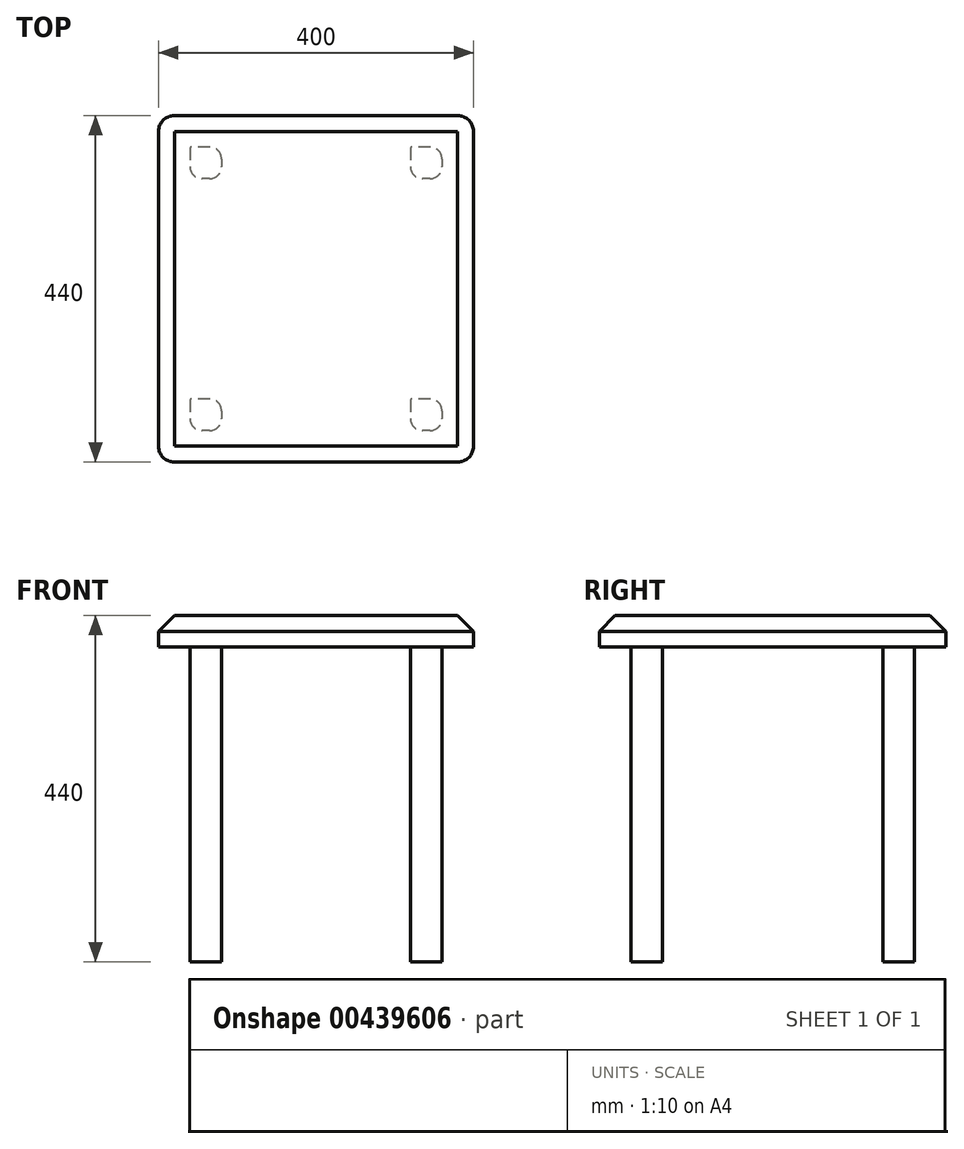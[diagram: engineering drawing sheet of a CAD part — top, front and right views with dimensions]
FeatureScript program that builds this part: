
annotation { "Feature Type Name" : "Feature", "Feature Type Description" : "" }
export const myFeature = defineFeature(function(context is Context, id is Id, definition is map)
    precondition{}
    {
        {
            var Q0;
            Q0=qCreatedBy(makeId("Top.planeOp"),FACE);
            var sketch = newSketch(context, id + "F0", { "sketchPlane" : qUnion([Q0])});
            skLineSegment(sketch, "E0.bottom", {"start": v(-177.18, 235.75) * mm, "end": v(182.82, 235.75) * mm});
            skLineSegment(sketch, "E0.top", {"start": v(-177.18, -204.25) * mm, "end": v(182.82, -204.25) * mm});
            skLineSegment(sketch, "E0.left", {"start": v(-197.18, 215.75) * mm, "end": v(-197.18, -184.25) * mm});
            skLineSegment(sketch, "E0.right", {"start": v(202.82, 215.75) * mm, "end": v(202.82, -184.25) * mm});
            skPoint(sketch, "E1.visualSharp", {"position": v(-197.18, 235.75) * mm});
            skArc(sketch, "E1.filletArc", {"start": v(-177.18, 235.75) * mm, "mid": v(-191.32, 229.9) * mm, "end": v(-197.18, 215.75) * mm});
            skPoint(sketch, "E2.visualSharp", {"position": v(202.82, 235.75) * mm});
            skArc(sketch, "E2.filletArc", {"start": v(202.82, 215.75) * mm, "mid": v(196.96, 229.9) * mm, "end": v(182.82, 235.75) * mm});
            skPoint(sketch, "E3.visualSharp", {"position": v(202.82, -204.25) * mm});
            skArc(sketch, "E3.filletArc", {"start": v(182.82, -204.25) * mm, "mid": v(196.96, -198.4) * mm, "end": v(202.82, -184.25) * mm});
            skPoint(sketch, "E4.visualSharp", {"position": v(-197.18, -204.25) * mm});
            skArc(sketch, "E4.filletArc", {"start": v(-197.18, -184.25) * mm, "mid": v(-191.32, -198.4) * mm, "end": v(-177.18, -204.25) * mm});
            skSolve(sketch);
        }
        {
            var Q0;
            Q0 = qSketchRegion(id + "F0", true);
            extrude(context, id + "F1", {"entities" : qUnion([Q0]), "depth" : 40 * mm});
        }
        {
            var Q0;
            Q0=makeQuery(id+"F1.opExtrude","CAP_FACE",FACE,{"disambiguationData":[OSD([sQuery(id+"F0.wireOp",EDGE,"E0.bottom"),sQuery(id+"F0.wireOp",EDGE,"E0.top"),sQuery(id+"F0.wireOp",EDGE,"E0.left"),sQuery(id+"F0.wireOp",EDGE,"E0.right"),sQuery(id+"F0.wireOp",EDGE,"E1.filletArc"),sQuery(id+"F0.wireOp",EDGE,"E2.filletArc"),sQuery(id+"F0.wireOp",EDGE,"E3.filletArc"),sQuery(id+"F0.wireOp",EDGE,"E4.filletArc")])],"isStart":true});
            var sketch = newSketch(context, id + "F2", { "sketchPlane" : qUnion([Q0])});
            skLineSegment(sketch, "E5.bottom", {"start": v(147.82, -195.75) * mm, "end": v(124.33, -195.75) * mm});
            skLineSegment(sketch, "E5.top", {"start": v(147.82, -155.75) * mm, "end": v(137.82, -155.75) * mm});
            skLineSegment(sketch, "E5.left", {"start": v(162.82, -180.75) * mm, "end": v(162.82, -170.75) * mm});
            skLineSegment(sketch, "E5.right", {"start": v(122.82, -194.24) * mm, "end": v(122.82, -170.75) * mm});
            skPoint(sketch, "E6.visualSharp", {"position": v(122.82, -195.75) * mm});
            skArc(sketch, "E6.filletArc", {"start": v(122.82, -194.24) * mm, "mid": v(123.26, -195.3) * mm, "end": v(124.33, -195.75) * mm});
            skPoint(sketch, "E7.visualSharp", {"position": v(162.82, -195.75) * mm});
            skArc(sketch, "E7.filletArc", {"start": v(147.82, -195.75) * mm, "mid": v(158.42, -191.36) * mm, "end": v(162.82, -180.75) * mm});
            skPoint(sketch, "E8.visualSharp", {"position": v(162.82, -155.75) * mm});
            skArc(sketch, "E8.filletArc", {"start": v(162.82, -170.75) * mm, "mid": v(158.42, -160.14) * mm, "end": v(147.82, -155.75) * mm});
            skPoint(sketch, "E9.visualSharp", {"position": v(122.82, -155.75) * mm});
            skArc(sketch, "E9.filletArc", {"start": v(137.82, -155.75) * mm, "mid": v(127.21, -160.14) * mm, "end": v(122.82, -170.75) * mm});
            skArc(sketch, "E10.0.1.0", {"start": v(147.82, 124.25) * mm, "mid": v(158.42, 128.64) * mm, "end": v(162.82, 139.25) * mm});
            skPoint(sketch, "E10.0.1.1", {"position": v(122.82, 124.25) * mm});
            skPoint(sketch, "E10.0.1.2", {"position": v(162.82, 124.25) * mm});
            skLineSegment(sketch, "E10.0.1.3", {"start": v(122.82, 125.76) * mm, "end": v(122.82, 149.25) * mm});
            skPoint(sketch, "E10.0.1.4", {"position": v(162.82, 164.25) * mm});
            skPoint(sketch, "E10.0.1.5", {"position": v(122.82, 164.25) * mm});
            skLineSegment(sketch, "E10.0.1.6", {"start": v(147.82, 124.25) * mm, "end": v(124.33, 124.25) * mm});
            skLineSegment(sketch, "E10.0.1.7", {"start": v(147.82, 164.25) * mm, "end": v(137.82, 164.25) * mm});
            skArc(sketch, "E10.0.1.8", {"start": v(162.82, 149.25) * mm, "mid": v(158.42, 159.86) * mm, "end": v(147.82, 164.25) * mm});
            skArc(sketch, "E10.0.1.9", {"start": v(137.82, 164.25) * mm, "mid": v(127.21, 159.86) * mm, "end": v(122.82, 149.25) * mm});
            skLineSegment(sketch, "E10.0.1.10", {"start": v(162.82, 139.25) * mm, "end": v(162.82, 149.25) * mm});
            skArc(sketch, "E10.0.1.11", {"start": v(122.82, 125.76) * mm, "mid": v(123.26, 124.7) * mm, "end": v(124.33, 124.25) * mm});
            skArc(sketch, "E10.1.0.0", {"start": v(-132.18, -195.75) * mm, "mid": v(-121.58, -191.36) * mm, "end": v(-117.18, -180.75) * mm});
            skPoint(sketch, "E10.1.0.1", {"position": v(-157.18, -195.75) * mm});
            skPoint(sketch, "E10.1.0.2", {"position": v(-117.18, -195.75) * mm});
            skLineSegment(sketch, "E10.1.0.3", {"start": v(-157.18, -194.24) * mm, "end": v(-157.18, -170.75) * mm});
            skPoint(sketch, "E10.1.0.4", {"position": v(-117.18, -155.75) * mm});
            skPoint(sketch, "E10.1.0.5", {"position": v(-157.18, -155.75) * mm});
            skLineSegment(sketch, "E10.1.0.6", {"start": v(-132.18, -195.75) * mm, "end": v(-155.67, -195.75) * mm});
            skLineSegment(sketch, "E10.1.0.7", {"start": v(-132.18, -155.75) * mm, "end": v(-142.18, -155.75) * mm});
            skArc(sketch, "E10.1.0.8", {"start": v(-117.18, -170.75) * mm, "mid": v(-121.58, -160.14) * mm, "end": v(-132.18, -155.75) * mm});
            skArc(sketch, "E10.1.0.9", {"start": v(-142.18, -155.75) * mm, "mid": v(-152.79, -160.14) * mm, "end": v(-157.18, -170.75) * mm});
            skLineSegment(sketch, "E10.1.0.10", {"start": v(-117.18, -180.75) * mm, "end": v(-117.18, -170.75) * mm});
            skArc(sketch, "E10.1.0.11", {"start": v(-157.18, -194.24) * mm, "mid": v(-156.74, -195.3) * mm, "end": v(-155.67, -195.75) * mm});
            skArc(sketch, "E10.1.1.0", {"start": v(-132.18, 124.25) * mm, "mid": v(-121.58, 128.64) * mm, "end": v(-117.18, 139.25) * mm});
            skPoint(sketch, "E10.1.1.1", {"position": v(-157.18, 124.25) * mm});
            skPoint(sketch, "E10.1.1.2", {"position": v(-117.18, 124.25) * mm});
            skLineSegment(sketch, "E10.1.1.3", {"start": v(-157.18, 125.76) * mm, "end": v(-157.18, 149.25) * mm});
            skPoint(sketch, "E10.1.1.4", {"position": v(-117.18, 164.25) * mm});
            skPoint(sketch, "E10.1.1.5", {"position": v(-157.18, 164.25) * mm});
            skLineSegment(sketch, "E10.1.1.6", {"start": v(-132.18, 124.25) * mm, "end": v(-155.67, 124.25) * mm});
            skLineSegment(sketch, "E10.1.1.7", {"start": v(-132.18, 164.25) * mm, "end": v(-142.18, 164.25) * mm});
            skArc(sketch, "E10.1.1.8", {"start": v(-117.18, 149.25) * mm, "mid": v(-121.58, 159.86) * mm, "end": v(-132.18, 164.25) * mm});
            skArc(sketch, "E10.1.1.9", {"start": v(-142.18, 164.25) * mm, "mid": v(-152.79, 159.86) * mm, "end": v(-157.18, 149.25) * mm});
            skLineSegment(sketch, "E10.1.1.10", {"start": v(-117.18, 139.25) * mm, "end": v(-117.18, 149.25) * mm});
            skArc(sketch, "E10.1.1.11", {"start": v(-157.18, 125.76) * mm, "mid": v(-156.74, 124.7) * mm, "end": v(-155.67, 124.25) * mm});
            skLineSegment(sketch, "E10.direction1", {"start": v(122.82, -195.75) * mm, "end": v(-157.18, -195.75) * mm, "construction": true});
            skLineSegment(sketch, "E10.direction2", {"start": v(122.82, -195.75) * mm, "end": v(122.82, 124.25) * mm, "construction": true});
            skSolve(sketch);
        }
        {
            var Q0;
            Q0=makeQuery(id+"F2.imprint","IMPRINT",FACE,{"disambiguationData":[TD([[makeQuery(id+"F2.imprint","IMPRINT",EDGE,{"derivedFrom":sQuery(id+"F2.wireOp",EDGE,"E10.1.0.0")}),1.0]])]});
            var Q1;
            Q1=makeQuery(id+"F2.imprint","IMPRINT",FACE,{"disambiguationData":[TD([[makeQuery(id+"F2.imprint","IMPRINT",EDGE,{"derivedFrom":sQuery(id+"F2.wireOp",EDGE,"E5.bottom")}),-1.0]])]});
            var Q2;
            Q2=makeQuery(id+"F2.imprint","IMPRINT",FACE,{"disambiguationData":[TD([[makeQuery(id+"F2.imprint","IMPRINT",EDGE,{"derivedFrom":sQuery(id+"F2.wireOp",EDGE,"E10.0.1.0")}),1.0]])]});
            var Q3;
            Q3=makeQuery(id+"F2.imprint","IMPRINT",FACE,{"disambiguationData":[TD([[makeQuery(id+"F2.imprint","IMPRINT",EDGE,{"derivedFrom":sQuery(id+"F2.wireOp",EDGE,"E10.1.1.0")}),1.0]])]});
            extrude(context, id + "F3", {"entities" : qUnion([Q0, Q1, Q2, Q3]), "operationType" : NewBodyOperationType.ADD, "depth" : 400 * mm});
        }
        {
            var Q0;
            Q0=makeQuery(id+"F1.opExtrude","CAP_FACE",FACE,{"disambiguationData":[OSD([sQuery(id+"F0.wireOp",EDGE,"E0.bottom"),sQuery(id+"F0.wireOp",EDGE,"E0.top"),sQuery(id+"F0.wireOp",EDGE,"E0.left"),sQuery(id+"F0.wireOp",EDGE,"E0.right"),sQuery(id+"F0.wireOp",EDGE,"E1.filletArc"),sQuery(id+"F0.wireOp",EDGE,"E2.filletArc"),sQuery(id+"F0.wireOp",EDGE,"E3.filletArc"),sQuery(id+"F0.wireOp",EDGE,"E4.filletArc")])],"isStart":false});
            chamfer(context, id + "F4", {"entities" : qUnion([Q0]), "width" : 20 * mm, "tangentPropagation" : true});
        }
    });
